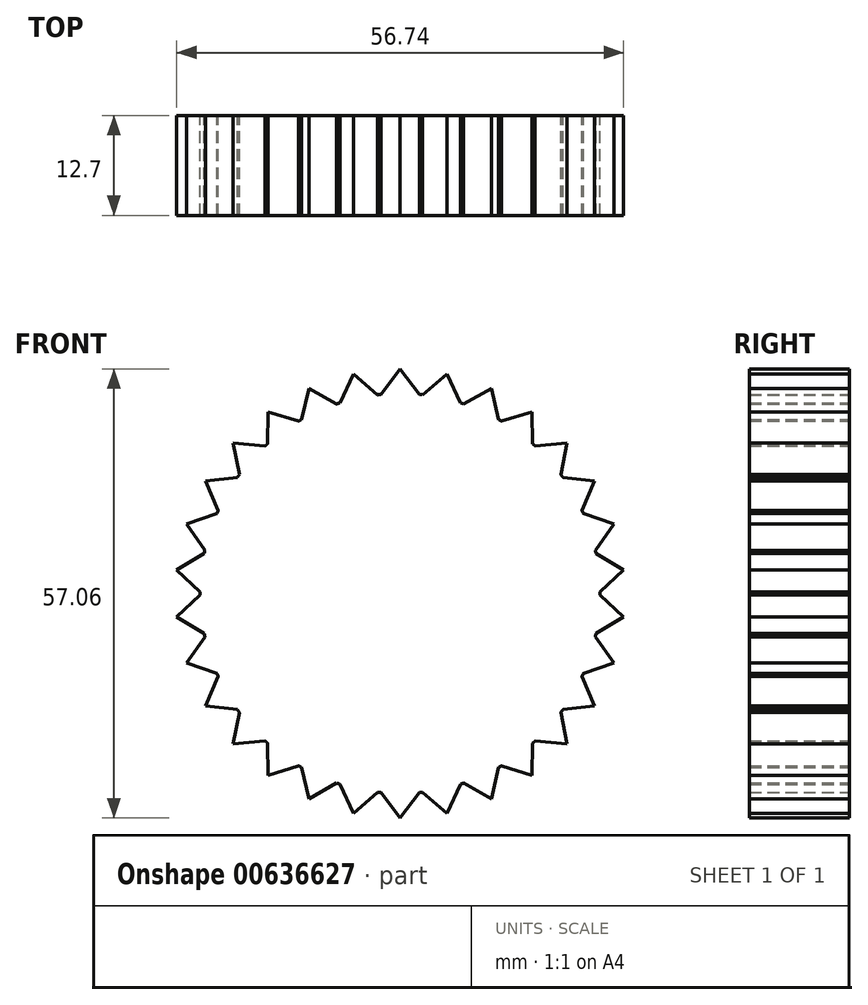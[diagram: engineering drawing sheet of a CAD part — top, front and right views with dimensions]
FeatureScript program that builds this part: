
annotation { "Feature Type Name" : "Feature", "Feature Type Description" : "" }
export const myFeature = defineFeature(function(context is Context, id is Id, definition is map)
    precondition{}
    {
        {
            var Q0;
            Q0=qCreatedBy(makeId("Front.planeOp"),FACE);
            var sketch = newSketch(context, id + "F0", { "sketchPlane" : qUnion([Q0])});
            skCircle(sketch, "E0", {"center": v(0, 0) * mm, "radius": 25.4 * mm});
            skLineSegment(sketch, "E1", {"start": v(0, 28.53) * mm, "end": v(0, 25.4) * mm, "construction": true});
            skLineSegment(sketch, "E2", {"start": v(0, 28.53) * mm, "end": v(-2.44, 25.28) * mm});
            skLineSegment(sketch, "E3", {"start": v(-2.44, 25.28) * mm, "end": v(0, 25.4) * mm});
            skLineSegment(sketch, "E4.MirrorCS", {"start": v(0, 28.53) * mm, "end": v(2.44, 25.28) * mm});
            skLineSegment(sketch, "E5.MirrorCS", {"start": v(2.44, 25.28) * mm, "end": v(0, 25.4) * mm});
            skLineSegment(sketch, "E6.anchor1", {"start": v(0, 0) * mm, "end": v(-2.44, 25.28) * mm, "construction": true});
            skLineSegment(sketch, "E6.anchor2", {"start": v(0, 0) * mm, "end": v(-2.44, 25.28) * mm, "construction": true});
            skLineSegment(sketch, "E7.1.0", {"start": v(-5.93, 27.9) * mm, "end": v(-7.65, 24.22) * mm});
            skLineSegment(sketch, "E7.1.1", {"start": v(-5.93, 27.9) * mm, "end": v(-2.87, 25.24) * mm});
            skLineSegment(sketch, "E7.1.2", {"start": v(-2.87, 25.24) * mm, "end": v(-5.28, 24.84) * mm});
            skLineSegment(sketch, "E7.1.3", {"start": v(-7.65, 24.22) * mm, "end": v(-5.28, 24.84) * mm});
            skLineSegment(sketch, "E7.2.0", {"start": v(-11.6, 26.06) * mm, "end": v(-12.52, 22.1) * mm});
            skLineSegment(sketch, "E7.2.1", {"start": v(-11.6, 26.06) * mm, "end": v(-8.05, 24.1) * mm});
            skLineSegment(sketch, "E7.2.2", {"start": v(-8.05, 24.1) * mm, "end": v(-10.33, 23.2) * mm});
            skLineSegment(sketch, "E7.2.3", {"start": v(-12.52, 22.1) * mm, "end": v(-10.33, 23.2) * mm});
            skLineSegment(sketch, "E7.3.0", {"start": v(-16.77, 23.08) * mm, "end": v(-16.84, 19.02) * mm});
            skLineSegment(sketch, "E7.3.1", {"start": v(-16.77, 23.08) * mm, "end": v(-12.88, 21.9) * mm});
            skLineSegment(sketch, "E7.3.2", {"start": v(-12.88, 21.9) * mm, "end": v(-14.93, 20.55) * mm});
            skLineSegment(sketch, "E7.3.3", {"start": v(-16.84, 19.02) * mm, "end": v(-14.93, 20.55) * mm});
            skLineSegment(sketch, "E7.4.0", {"start": v(-21.2, 19.09) * mm, "end": v(-20.42, 15.1) * mm});
            skLineSegment(sketch, "E7.4.1", {"start": v(-21.2, 19.09) * mm, "end": v(-17.15, 18.73) * mm});
            skLineSegment(sketch, "E7.4.2", {"start": v(-17.15, 18.73) * mm, "end": v(-18.88, 17) * mm});
            skLineSegment(sketch, "E7.4.3", {"start": v(-20.42, 15.1) * mm, "end": v(-18.88, 17) * mm});
            skLineSegment(sketch, "E7.5.0", {"start": v(-24.7, 14.26) * mm, "end": v(-23.12, 10.52) * mm});
            skLineSegment(sketch, "E7.5.1", {"start": v(-24.7, 14.26) * mm, "end": v(-20.67, 14.76) * mm});
            skLineSegment(sketch, "E7.5.2", {"start": v(-20.67, 14.76) * mm, "end": v(-22, 12.7) * mm});
            skLineSegment(sketch, "E7.5.3", {"start": v(-23.12, 10.52) * mm, "end": v(-22, 12.7) * mm});
            skLineSegment(sketch, "E7.6.0", {"start": v(-27.13, 8.82) * mm, "end": v(-24.8, 5.49) * mm});
            skLineSegment(sketch, "E7.6.1", {"start": v(-27.13, 8.82) * mm, "end": v(-23.29, 10.14) * mm});
            skLineSegment(sketch, "E7.6.2", {"start": v(-23.29, 10.14) * mm, "end": v(-24.16, 7.85) * mm});
            skLineSegment(sketch, "E7.6.3", {"start": v(-24.8, 5.49) * mm, "end": v(-24.16, 7.85) * mm});
            skLineSegment(sketch, "E7.7.0", {"start": v(-28.37, 2.98) * mm, "end": v(-25.4, 0.21) * mm});
            skLineSegment(sketch, "E7.7.1", {"start": v(-28.37, 2.98) * mm, "end": v(-24.89, 5.07) * mm});
            skLineSegment(sketch, "E7.7.2", {"start": v(-24.89, 5.07) * mm, "end": v(-25.26, 2.66) * mm});
            skLineSegment(sketch, "E7.7.3", {"start": v(-25.4, 0.21) * mm, "end": v(-25.26, 2.66) * mm});
            skLineSegment(sketch, "E7.8.0", {"start": v(-28.37, -2.98) * mm, "end": v(-24.89, -5.07) * mm});
            skLineSegment(sketch, "E7.8.1", {"start": v(-28.37, -2.98) * mm, "end": v(-25.4, -0.21) * mm});
            skLineSegment(sketch, "E7.8.2", {"start": v(-25.4, -0.21) * mm, "end": v(-25.26, -2.66) * mm});
            skLineSegment(sketch, "E7.8.3", {"start": v(-24.89, -5.07) * mm, "end": v(-25.26, -2.66) * mm});
            skLineSegment(sketch, "E7.9.0", {"start": v(-27.13, -8.82) * mm, "end": v(-23.29, -10.14) * mm});
            skLineSegment(sketch, "E7.9.1", {"start": v(-27.13, -8.82) * mm, "end": v(-24.8, -5.49) * mm});
            skLineSegment(sketch, "E7.9.2", {"start": v(-24.8, -5.49) * mm, "end": v(-24.16, -7.85) * mm});
            skLineSegment(sketch, "E7.9.3", {"start": v(-23.29, -10.14) * mm, "end": v(-24.16, -7.85) * mm});
            skLineSegment(sketch, "E7.10.0", {"start": v(-24.7, -14.26) * mm, "end": v(-20.67, -14.76) * mm});
            skLineSegment(sketch, "E7.10.1", {"start": v(-24.7, -14.26) * mm, "end": v(-23.12, -10.52) * mm});
            skLineSegment(sketch, "E7.10.2", {"start": v(-23.12, -10.52) * mm, "end": v(-22, -12.7) * mm});
            skLineSegment(sketch, "E7.10.3", {"start": v(-20.67, -14.76) * mm, "end": v(-22, -12.7) * mm});
            skLineSegment(sketch, "E7.11.0", {"start": v(-21.2, -19.09) * mm, "end": v(-17.15, -18.73) * mm});
            skLineSegment(sketch, "E7.11.1", {"start": v(-21.2, -19.09) * mm, "end": v(-20.42, -15.1) * mm});
            skLineSegment(sketch, "E7.11.2", {"start": v(-20.42, -15.1) * mm, "end": v(-18.88, -17) * mm});
            skLineSegment(sketch, "E7.11.3", {"start": v(-17.15, -18.73) * mm, "end": v(-18.88, -17) * mm});
            skLineSegment(sketch, "E7.12.0", {"start": v(-16.77, -23.08) * mm, "end": v(-12.88, -21.9) * mm});
            skLineSegment(sketch, "E7.12.1", {"start": v(-16.77, -23.08) * mm, "end": v(-16.84, -19.02) * mm});
            skLineSegment(sketch, "E7.12.2", {"start": v(-16.84, -19.02) * mm, "end": v(-14.93, -20.55) * mm});
            skLineSegment(sketch, "E7.12.3", {"start": v(-12.88, -21.9) * mm, "end": v(-14.93, -20.55) * mm});
            skLineSegment(sketch, "E7.13.0", {"start": v(-11.6, -26.06) * mm, "end": v(-8.05, -24.1) * mm});
            skLineSegment(sketch, "E7.13.1", {"start": v(-11.6, -26.06) * mm, "end": v(-12.52, -22.1) * mm});
            skLineSegment(sketch, "E7.13.2", {"start": v(-12.52, -22.1) * mm, "end": v(-10.33, -23.2) * mm});
            skLineSegment(sketch, "E7.13.3", {"start": v(-8.05, -24.1) * mm, "end": v(-10.33, -23.2) * mm});
            skLineSegment(sketch, "E7.14.0", {"start": v(-5.93, -27.9) * mm, "end": v(-2.87, -25.24) * mm});
            skLineSegment(sketch, "E7.14.1", {"start": v(-5.93, -27.9) * mm, "end": v(-7.65, -24.22) * mm});
            skLineSegment(sketch, "E7.14.2", {"start": v(-7.65, -24.22) * mm, "end": v(-5.28, -24.84) * mm});
            skLineSegment(sketch, "E7.14.3", {"start": v(-2.87, -25.24) * mm, "end": v(-5.28, -24.84) * mm});
            skLineSegment(sketch, "E7.15.0", {"start": v(0, -28.53) * mm, "end": v(2.44, -25.28) * mm});
            skLineSegment(sketch, "E7.15.1", {"start": v(0, -28.53) * mm, "end": v(-2.44, -25.28) * mm});
            skLineSegment(sketch, "E7.15.2", {"start": v(-2.44, -25.28) * mm, "end": v(0, -25.4) * mm});
            skLineSegment(sketch, "E7.15.3", {"start": v(2.44, -25.28) * mm, "end": v(0, -25.4) * mm});
            skLineSegment(sketch, "E7.16.0", {"start": v(5.93, -27.9) * mm, "end": v(7.65, -24.22) * mm});
            skLineSegment(sketch, "E7.16.1", {"start": v(5.93, -27.9) * mm, "end": v(2.87, -25.24) * mm});
            skLineSegment(sketch, "E7.16.2", {"start": v(2.87, -25.24) * mm, "end": v(5.28, -24.84) * mm});
            skLineSegment(sketch, "E7.16.3", {"start": v(7.65, -24.22) * mm, "end": v(5.28, -24.84) * mm});
            skLineSegment(sketch, "E7.17.0", {"start": v(11.6, -26.06) * mm, "end": v(12.52, -22.1) * mm});
            skLineSegment(sketch, "E7.17.1", {"start": v(11.6, -26.06) * mm, "end": v(8.05, -24.1) * mm});
            skLineSegment(sketch, "E7.17.2", {"start": v(8.05, -24.1) * mm, "end": v(10.33, -23.2) * mm});
            skLineSegment(sketch, "E7.17.3", {"start": v(12.52, -22.1) * mm, "end": v(10.33, -23.2) * mm});
            skLineSegment(sketch, "E7.18.0", {"start": v(16.77, -23.08) * mm, "end": v(16.84, -19.02) * mm});
            skLineSegment(sketch, "E7.18.1", {"start": v(16.77, -23.08) * mm, "end": v(12.88, -21.9) * mm});
            skLineSegment(sketch, "E7.18.2", {"start": v(12.88, -21.9) * mm, "end": v(14.93, -20.55) * mm});
            skLineSegment(sketch, "E7.18.3", {"start": v(16.84, -19.02) * mm, "end": v(14.93, -20.55) * mm});
            skLineSegment(sketch, "E7.19.0", {"start": v(21.2, -19.09) * mm, "end": v(20.42, -15.1) * mm});
            skLineSegment(sketch, "E7.19.1", {"start": v(21.2, -19.09) * mm, "end": v(17.15, -18.73) * mm});
            skLineSegment(sketch, "E7.19.2", {"start": v(17.15, -18.73) * mm, "end": v(18.88, -17) * mm});
            skLineSegment(sketch, "E7.19.3", {"start": v(20.42, -15.1) * mm, "end": v(18.88, -17) * mm});
            skLineSegment(sketch, "E7.20.0", {"start": v(24.7, -14.26) * mm, "end": v(23.12, -10.52) * mm});
            skLineSegment(sketch, "E7.20.1", {"start": v(24.7, -14.26) * mm, "end": v(20.67, -14.76) * mm});
            skLineSegment(sketch, "E7.20.2", {"start": v(20.67, -14.76) * mm, "end": v(22, -12.7) * mm});
            skLineSegment(sketch, "E7.20.3", {"start": v(23.12, -10.52) * mm, "end": v(22, -12.7) * mm});
            skLineSegment(sketch, "E7.21.0", {"start": v(27.13, -8.82) * mm, "end": v(24.8, -5.49) * mm});
            skLineSegment(sketch, "E7.21.1", {"start": v(27.13, -8.82) * mm, "end": v(23.29, -10.14) * mm});
            skLineSegment(sketch, "E7.21.2", {"start": v(23.29, -10.14) * mm, "end": v(24.16, -7.85) * mm});
            skLineSegment(sketch, "E7.21.3", {"start": v(24.8, -5.49) * mm, "end": v(24.16, -7.85) * mm});
            skLineSegment(sketch, "E7.22.0", {"start": v(28.37, -2.98) * mm, "end": v(25.4, -0.21) * mm});
            skLineSegment(sketch, "E7.22.1", {"start": v(28.37, -2.98) * mm, "end": v(24.89, -5.07) * mm});
            skLineSegment(sketch, "E7.22.2", {"start": v(24.89, -5.07) * mm, "end": v(25.26, -2.66) * mm});
            skLineSegment(sketch, "E7.22.3", {"start": v(25.4, -0.21) * mm, "end": v(25.26, -2.66) * mm});
            skLineSegment(sketch, "E7.23.0", {"start": v(28.37, 2.98) * mm, "end": v(24.89, 5.07) * mm});
            skLineSegment(sketch, "E7.23.1", {"start": v(28.37, 2.98) * mm, "end": v(25.4, 0.21) * mm});
            skLineSegment(sketch, "E7.23.2", {"start": v(25.4, 0.21) * mm, "end": v(25.26, 2.66) * mm});
            skLineSegment(sketch, "E7.23.3", {"start": v(24.89, 5.07) * mm, "end": v(25.26, 2.66) * mm});
            skLineSegment(sketch, "E7.24.0", {"start": v(27.13, 8.82) * mm, "end": v(23.29, 10.14) * mm});
            skLineSegment(sketch, "E7.24.1", {"start": v(27.13, 8.82) * mm, "end": v(24.8, 5.49) * mm});
            skLineSegment(sketch, "E7.24.2", {"start": v(24.8, 5.49) * mm, "end": v(24.16, 7.85) * mm});
            skLineSegment(sketch, "E7.24.3", {"start": v(23.29, 10.14) * mm, "end": v(24.16, 7.85) * mm});
            skLineSegment(sketch, "E7.25.0", {"start": v(24.7, 14.26) * mm, "end": v(20.67, 14.76) * mm});
            skLineSegment(sketch, "E7.25.1", {"start": v(24.7, 14.26) * mm, "end": v(23.12, 10.52) * mm});
            skLineSegment(sketch, "E7.25.2", {"start": v(23.12, 10.52) * mm, "end": v(22, 12.7) * mm});
            skLineSegment(sketch, "E7.25.3", {"start": v(20.67, 14.76) * mm, "end": v(22, 12.7) * mm});
            skLineSegment(sketch, "E7.26.0", {"start": v(21.2, 19.09) * mm, "end": v(17.15, 18.73) * mm});
            skLineSegment(sketch, "E7.26.1", {"start": v(21.2, 19.09) * mm, "end": v(20.42, 15.1) * mm});
            skLineSegment(sketch, "E7.26.2", {"start": v(20.42, 15.1) * mm, "end": v(18.88, 17) * mm});
            skLineSegment(sketch, "E7.26.3", {"start": v(17.15, 18.73) * mm, "end": v(18.88, 17) * mm});
            skLineSegment(sketch, "E7.27.0", {"start": v(16.77, 23.08) * mm, "end": v(12.88, 21.9) * mm});
            skLineSegment(sketch, "E7.27.1", {"start": v(16.77, 23.08) * mm, "end": v(16.84, 19.02) * mm});
            skLineSegment(sketch, "E7.27.2", {"start": v(16.84, 19.02) * mm, "end": v(14.93, 20.55) * mm});
            skLineSegment(sketch, "E7.27.3", {"start": v(12.88, 21.9) * mm, "end": v(14.93, 20.55) * mm});
            skLineSegment(sketch, "E7.28.0", {"start": v(11.6, 26.06) * mm, "end": v(8.05, 24.1) * mm});
            skLineSegment(sketch, "E7.28.1", {"start": v(11.6, 26.06) * mm, "end": v(12.52, 22.1) * mm});
            skLineSegment(sketch, "E7.28.2", {"start": v(12.52, 22.1) * mm, "end": v(10.33, 23.2) * mm});
            skLineSegment(sketch, "E7.28.3", {"start": v(8.05, 24.1) * mm, "end": v(10.33, 23.2) * mm});
            skLineSegment(sketch, "E7.29.0", {"start": v(5.93, 27.9) * mm, "end": v(2.87, 25.24) * mm});
            skLineSegment(sketch, "E7.29.1", {"start": v(5.93, 27.9) * mm, "end": v(7.65, 24.22) * mm});
            skLineSegment(sketch, "E7.29.2", {"start": v(7.65, 24.22) * mm, "end": v(5.28, 24.84) * mm});
            skLineSegment(sketch, "E7.29.3", {"start": v(2.87, 25.24) * mm, "end": v(5.28, 24.84) * mm});
            skSolve(sketch);
        }
        {
            var Q0;
            Q0 = qSketchRegion(id + "F0", true);
            extrude(context, id + "F1", {"entities" : qUnion([Q0]), "depth" : 12.7 * mm, "offsetDistance" : 25.4 * mm});
        }
    });
